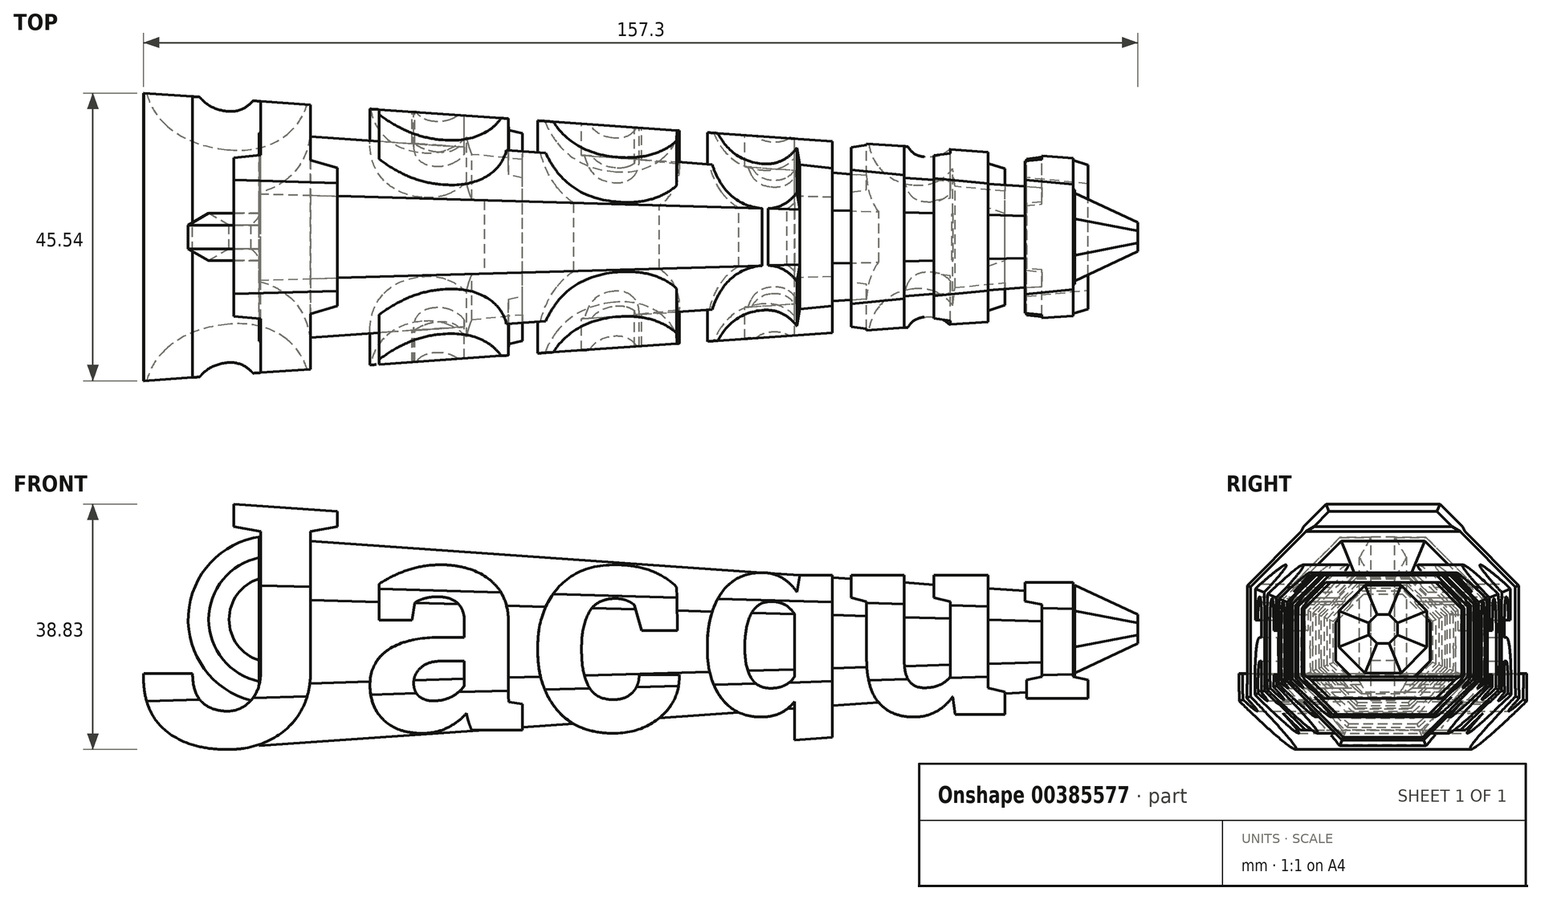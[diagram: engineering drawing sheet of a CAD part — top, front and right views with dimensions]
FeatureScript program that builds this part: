
annotation { "Feature Type Name" : "Feature", "Feature Type Description" : "" }
export const myFeature = defineFeature(function(context is Context, id is Id, definition is map)
    precondition{}
    {
        {
            assignVariable(context, id + "F0", {"name" : "hookPlane", "anyValue" : 55});
        }
        {
            var Q0;
            Q0=qCreatedBy(makeId("Front.planeOp"),FACE);
            var sketch = newSketch(context, id + "F1", { "sketchPlane" : qUnion([Q0])});
            skText(sketch, "E0", { "text": "J", "fontName": "RobotoSlab-Bold.ttf"});
            skPoint(sketch, "E1", {"position": v(-41.23, 0) * mm});
            skText(sketch, "E2", { "text": "ac", "fontName": "RobotoSlab-Bold.ttf"});
            skText(sketch, "E3", { "text": "qu", "fontName": "RobotoSlab-Bold.ttf"});
            skText(sketch, "E4", { "text": "i", "fontName": "RobotoSlab-Bold.ttf"});
            skPoint(sketch, "E5", {"position": v(12.52, 0) * mm});
            skPoint(sketch, "E6", {"position": v(63.49, 0) * mm});
            skLineSegment(sketch, "E7", {"start": v(-76.24, -20) * mm, "end": v(-76.24, -51.65) * mm, "construction": true});
            skLineSegment(sketch, "E8", {"start": v(-76.24, -51.65) * mm, "end": v(76.24, -51.65) * mm, "construction": true});
            skLineSegment(sketch, "E9", {"start": v(76.24, -51.65) * mm, "end": v(76.24, -12.5) * mm, "construction": true});
            skPoint(sketch, "E10", {"position": v(0, -51.65) * mm});
            const initialGuessF1  = {"E0": [-0.07624, -0.02, 1, 0, 0.04], "E2": [-0.04123, -0.0175, 1, 0, 0.035], "E3": [0.01252, -0.015, 1, 0, 0.03], "E4": [0.06349, -0.0125, 1, 0, 0.025]};
            skSetInitialGuess(sketch, initialGuessF1);
            skSolve(sketch);
        }
        {
            var Q0;
            Q0=qSketchRegion(id+"F1",true);
            extrude(context, id + "F2", {"entities" : qUnion([Q0]), "depth" : 25 * mm, "hasSecondDirection" : true, "secondDirectionOppositeDirection" : true, "secondDirectionDepth" : 25 * mm});
        }
        {
            var Q0;
            Q0=qCreatedBy(makeId("Right.planeOp"),FACE);
            var sketch = newSketch(context, id + "F3", { "sketchPlane" : qUnion([Q0])});
            skCircle(sketch, "E11", {"center": v(0, -3.5) * mm, "radius": 12.5 * mm, "construction": true});
            skLineSegment(sketch, "E12", {"start": v(0, 19.5) * mm, "end": v(0, -8.52) * mm, "construction": true});
            skLineSegment(sketch, "E13.0", {"start": v(-5.18, 9) * mm, "end": v(5.18, 9) * mm});
            skLineSegment(sketch, "E13.1", {"start": v(5.18, 9) * mm, "end": v(12.5, 1.67) * mm});
            skLineSegment(sketch, "E13.2", {"start": v(12.5, 1.67) * mm, "end": v(12.5, -8.68) * mm});
            skLineSegment(sketch, "E13.3", {"start": v(12.5, -8.68) * mm, "end": v(5.18, -16) * mm});
            skLineSegment(sketch, "E13.4", {"start": v(5.18, -16) * mm, "end": v(-5.18, -16) * mm});
            skLineSegment(sketch, "E13.5", {"start": v(-5.18, -16) * mm, "end": v(-12.5, -8.68) * mm});
            skLineSegment(sketch, "E13.6", {"start": v(-12.5, -8.68) * mm, "end": v(-12.5, 1.67) * mm});
            skLineSegment(sketch, "E13.7", {"start": v(-12.5, 1.67) * mm, "end": v(-5.18, 9) * mm});
            skPoint(sketch, "E13.0.midPoint", {"position": v(0, 9) * mm});
            skSolve(sketch);
        }
        {
            var Q0;
            Q0=qSketchRegion(id+"F3",true);
            var Q1;
            Q1=makeQuery(id+"F2.opExtrude","SWEPT_FACE",FACE,{"disambiguationData":[OSD([sQuery(id+"F1.wireOp",EDGE,"E4.sketch_text.stroke-1")])]});
            extrude(context, id + "F4", {"entities" : qUnion([Q0]), "operationType" : NewBodyOperationType.ADD, "oppositeDirection" : true, "depth" : 57 * mm, "hasDraft" : true, "draftAngle" : 4 * degree, "hasSecondDirection" : true, "secondDirectionOppositeDirection" : false, "secondDirectionBoundEntityFace" : qUnion([Q1]), "secondDirectionDepth" : 72 * mm, "hasSecondDirectionDraft" : true, "secondDirectionDraftAngle" : 4 * degree, "secondDirectionDraftPullDirection" : true});
        }
        {
            var Q0;
            Q0=qCreatedBy(makeId("Right.planeOp"),FACE);
            var sketch = newSketch(context, id + "F5", { "sketchPlane" : qUnion([Q0])});
            skCircle(sketch, "E14.cCircle", {"center": v(0, -3.5) * mm, "radius": 17.5 * mm, "construction": true});
            skLineSegment(sketch, "E14.0", {"start": v(-7.25, 14) * mm, "end": v(7.25, 14) * mm});
            skLineSegment(sketch, "E14.1", {"start": v(7.25, 14) * mm, "end": v(17.5, 3.75) * mm});
            skLineSegment(sketch, "E14.2", {"start": v(17.5, 3.75) * mm, "end": v(17.5, -10.75) * mm});
            skLineSegment(sketch, "E14.3", {"start": v(17.5, -10.75) * mm, "end": v(7.25, -21) * mm});
            skLineSegment(sketch, "E14.4", {"start": v(7.25, -21) * mm, "end": v(-7.25, -21) * mm});
            skLineSegment(sketch, "E14.5", {"start": v(-7.25, -21) * mm, "end": v(-17.5, -10.75) * mm});
            skLineSegment(sketch, "E14.6", {"start": v(-17.5, -10.75) * mm, "end": v(-17.5, 3.75) * mm});
            skLineSegment(sketch, "E14.7", {"start": v(-17.5, 3.75) * mm, "end": v(-7.25, 14) * mm});
            skPoint(sketch, "E14.0.midPoint", {"position": v(0, 14) * mm});
            skLineSegment(sketch, "E15.bottom", {"start": v(40.52, 34.35) * mm, "end": v(-40.52, 34.35) * mm});
            skLineSegment(sketch, "E15.top", {"start": v(40.52, -41.36) * mm, "end": v(-40.52, -41.36) * mm});
            skLineSegment(sketch, "E15.left", {"start": v(40.52, 34.35) * mm, "end": v(40.52, -41.36) * mm});
            skLineSegment(sketch, "E15.right", {"start": v(-40.52, 34.35) * mm, "end": v(-40.52, -41.36) * mm});
            skLineSegment(sketch, "E16", {"start": v(0, 19.5) * mm, "end": v(0, -8.52) * mm, "construction": true});
            skSolve(sketch);
        }
        {
            var Q0;
            Q0=makeQuery(id+"F5.imprint","IMPRINT",FACE,{"disambiguationData":[TD([[makeQuery(id+"F5.imprint","IMPRINT",EDGE,{"derivedFrom":sQuery(id+"F5.wireOp",EDGE,"E14.0")}),1.0]])]});
            extrude(context, id + "F6", {"entities" : qUnion([Q0]), "operationType" : NewBodyOperationType.REMOVE, "endBound" : BoundingType.THROUGH_ALL, "depth" : 25 * mm, "hasDraft" : true, "draftAngle" : 4 * degree, "hasSecondDirection" : true, "secondDirectionBound" : SecondDirectionBoundingType.THROUGH_ALL, "secondDirectionOppositeDirection" : true, "secondDirectionDepth" : 25 * mm, "hasSecondDirectionDraft" : true, "secondDirectionDraftAngle" : 4 * degree, "secondDirectionDraftPullDirection" : true});
        }
        {
            var Q0;
            {var subQ0=sQuery(id+"F3.wireOp",EDGE,"E13.3");var subQ1=sQuery(id+"F3.wireOp",EDGE,"E13.2");var subQ2=sQuery(id+"F3.wireOp",EDGE,"E13.4");var subQ3=sQuery(id+"F3.wireOp",EDGE,"E13.5");var subQ4=sQuery(id+"F3.wireOp",EDGE,"E13.6");Q0=makeQuery(id+"F4.boolean.opBoolean","SPLIT",FACE,{"disambiguationData":[TD([makeQuery(id+"F2.opExtrude","SWEPT_FACE",FACE,{"disambiguationData":[OSD([sQuery(id+"F1.wireOp",EDGE,"E4.sketch_text.stroke-0")])]})])],"derivedFrom":makeQuery(id+"F4.opExtrude","CAP_FACE",FACE,{"disambiguationData":[OSD([sQuery(id+"F3.wireOp",EDGE,"E13.0"),sQuery(id+"F3.wireOp",EDGE,"E13.1"),subQ1,subQ0,subQ2,subQ3,subQ4,sQuery(id+"F3.wireOp",EDGE,"E13.7")])],"isStart":true})});}
            var sketch = newSketch(context, id + "F7", { "sketchPlane" : qUnion([Q0])});
            skCircle(sketch, "E17.cCircle", {"center": v(0, -1.5) * mm, "radius": 6.94 * mm, "construction": true});
            skLineSegment(sketch, "E17.0", {"start": v(-2.88, 5.44) * mm, "end": v(2.88, 5.44) * mm});
            skLineSegment(sketch, "E17.1", {"start": v(2.88, 5.44) * mm, "end": v(6.94, 1.37) * mm});
            skLineSegment(sketch, "E17.2", {"start": v(6.94, 1.37) * mm, "end": v(6.94, -4.38) * mm});
            skLineSegment(sketch, "E17.3", {"start": v(6.94, -4.38) * mm, "end": v(2.88, -8.45) * mm});
            skLineSegment(sketch, "E17.4", {"start": v(2.88, -8.45) * mm, "end": v(-2.88, -8.45) * mm});
            skLineSegment(sketch, "E17.5", {"start": v(-2.88, -8.45) * mm, "end": v(-6.94, -4.38) * mm});
            skLineSegment(sketch, "E17.6", {"start": v(-6.94, -4.38) * mm, "end": v(-6.94, 1.37) * mm});
            skLineSegment(sketch, "E17.7", {"start": v(-6.94, 1.37) * mm, "end": v(-2.88, 5.44) * mm});
            skPoint(sketch, "E17.0.midPoint", {"position": v(0, 5.44) * mm});
            skLineSegment(sketch, "E18", {"start": v(0, 19.59) * mm, "end": v(0, -20.57) * mm, "construction": true});
            skSolve(sketch);
        }
        {
            var Q0;
            Q0=qSketchRegion(id+"F7",true);
            extrude(context, id + "F8", {"entities" : qUnion([Q0]), "operationType" : NewBodyOperationType.ADD, "depth" : 10 * mm, "hasDraft" : true, "draftAngle" : 25 * degree, "draftPullDirection" : true});
        }
        {
            var Q0;
            Q0=qCreatedBy(makeId("Right.planeOp"),FACE);
            cPlane(context, id + "F9", {"entities" : qUnion([Q0]), "cplaneType" : CPlaneType.OFFSET, "offset" : (getVariable(context, 'hookPlane')) * mm, "oppositeDirection" : true, "width" : 150 * mm, "height" : 150 * mm});
        }
        {
            var Q0;
            Q0=qCreatedBy(makeId("Front.planeOp"),FACE);
            var sketch = newSketch(context, id + "F10", { "sketchPlane" : qUnion([Q0])});
            skArc(sketch, "E19", {"start": v(-50, 8.66) * mm, "mid": v(-65, 0) * mm, "end": v(-50, -8.66) * mm});
            skSolve(sketch);
        }
        {
            var Q0;
            Q0=qCreatedBy(id+"F9.planeOp",FACE);
            var sketch = newSketch(context, id + "F11", { "sketchPlane" : qUnion([Q0])});
            skCircle(sketch, "E20.cCircle", {"center": v(0, 10) * mm, "radius": 3.23 * mm, "construction": true});
            skLineSegment(sketch, "E20.0", {"start": v(1.87, 6.77) * mm, "end": v(-1.87, 6.77) * mm});
            skLineSegment(sketch, "E20.1", {"start": v(-1.87, 6.77) * mm, "end": v(-3.73, 10) * mm});
            skLineSegment(sketch, "E20.2", {"start": v(-3.73, 10) * mm, "end": v(-1.87, 13.23) * mm});
            skLineSegment(sketch, "E20.3", {"start": v(-1.87, 13.23) * mm, "end": v(1.87, 13.23) * mm});
            skLineSegment(sketch, "E20.4", {"start": v(1.87, 13.23) * mm, "end": v(3.73, 10) * mm});
            skLineSegment(sketch, "E20.5", {"start": v(3.73, 10) * mm, "end": v(1.87, 6.77) * mm});
            skPoint(sketch, "E20.0.midPoint", {"position": v(0, 6.77) * mm});
            skSolve(sketch);
        }
        {
            var Q0;
            Q0=qSketchRegion(id+"F11",true);
            var Q1;
            Q1=qConstructionFilter(qBodyType(qCreatedBy(id+"F10",EDGE),BodyType.WIRE),ConstructionObject.NO);
            sweep(context, id + "F12", {"operationType" : NewBodyOperationType.ADD, "profiles" : qUnion([Q0]), "path" : qUnion([Q1])});
        }
    });
